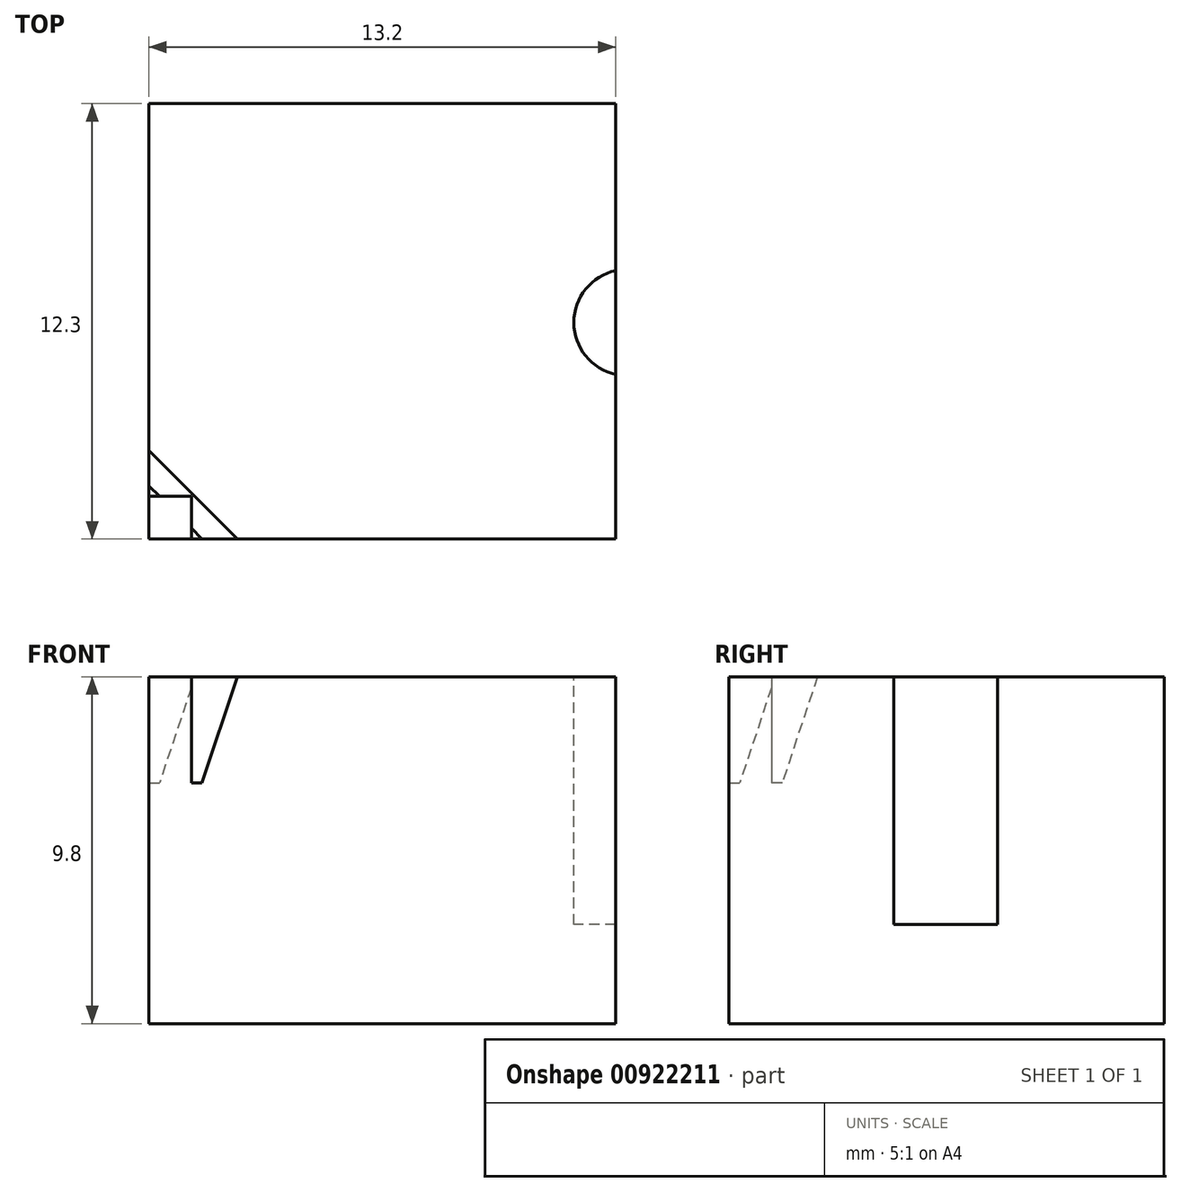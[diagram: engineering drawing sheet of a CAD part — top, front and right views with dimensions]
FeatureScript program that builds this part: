
annotation { "Feature Type Name" : "Feature", "Feature Type Description" : "" }
export const myFeature = defineFeature(function(context is Context, id is Id, definition is map)
    precondition{}
    {
        {
            var Q0;
            Q0=qCreatedBy(makeId("Top.planeOp"),FACE);
            var sketch = newSketch(context, id + "F0", { "sketchPlane" : qUnion([Q0])});
            skLineSegment(sketch, "E0.bottom", {"start": v(-6.6, 6.15) * mm, "end": v(6.6, 6.15) * mm});
            skLineSegment(sketch, "E0.top", {"start": v(-6.6, -6.15) * mm, "end": v(6.6, -6.15) * mm});
            skLineSegment(sketch, "E0.left", {"start": v(-6.6, 6.15) * mm, "end": v(-6.6, -6.15) * mm});
            skLineSegment(sketch, "E0.right", {"start": v(6.6, 6.15) * mm, "end": v(6.6, -6.15) * mm});
            skPoint(sketch, "E0.middle", {"position": v(0, 0) * mm});
            skSolve(sketch);
        }
        {
            var Q0;
            Q0 = qSketchRegion(id + "F0", true);
            extrude(context, id + "F1", {"entities" : qUnion([Q0]), "depth" : 9.8 * mm, "offsetDistance" : 25 * mm});
        }
        {
            var Q0;
            Q0=qCreatedBy(makeId("Top.planeOp"),FACE);
            cPlane(context, id + "F2", {"entities" : qUnion([Q0]), "cplaneType" : CPlaneType.OFFSET, "offset" : 6.8 * mm, "width" : 150 * mm, "height" : 150 * mm});
        }
        {
            var Q0;
            Q0=makeQuery(id+"F1.opExtrude","CAP_FACE",FACE,{"disambiguationData":[OSD([sQuery(id+"F0.wireOp",EDGE,"E0.bottom"),sQuery(id+"F0.wireOp",EDGE,"E0.top"),sQuery(id+"F0.wireOp",EDGE,"E0.left"),sQuery(id+"F0.wireOp",EDGE,"E0.right")])],"isStart":false});
            var sketch = newSketch(context, id + "F3", { "sketchPlane" : qUnion([Q0])});
            skLineSegment(sketch, "E1", {"start": v(-6.6, -6.15) * mm, "end": v(-4.1, -6.15) * mm});
            skLineSegment(sketch, "E2", {"start": v(-4.1, -6.15) * mm, "end": v(-6.6, -3.65) * mm});
            skLineSegment(sketch, "E3", {"start": v(-6.6, -3.65) * mm, "end": v(-6.6, -6.15) * mm});
            skSolve(sketch);
        }
        {
            var Q0;
            Q0=qCreatedBy(id+"F2.planeOp",FACE);
            var sketch = newSketch(context, id + "F4", { "sketchPlane" : qUnion([Q0])});
            skLineSegment(sketch, "E4", {"start": v(-5.1, -6.15) * mm, "end": v(-6.6, -4.65) * mm});
            skLineSegment(sketch, "E5", {"start": v(-6.6, -4.65) * mm, "end": v(-6.6, -6.15) * mm});
            skLineSegment(sketch, "E6", {"start": v(-6.6, -6.15) * mm, "end": v(-5.1, -6.15) * mm});
            skSolve(sketch);
        }
        {
            var Q1;
            Q1 = qSketchRegion(id + "F3", true);
            var Q2;
            Q2 = qSketchRegion(id + "F4", true);
            loft(context, id + "F5", {"operationType" : NewBodyOperationType.REMOVE, "sheetProfilesArray" : [{ "sheetProfileEntities" : qUnion([Q1]) }, { "sheetProfileEntities" : qUnion([Q2]) }]});
        }
        {
            var Q0;
            Q0=makeQuery(id+"F5.boolean.opBoolean","COPY",FACE,{"derivedFrom":makeQuery(id+"F5.opLoft","CAP_FACE",FACE,{"disambiguationData":[OSD([makeQuery(id+"F4.imprint","IMPRINT",FACE,{"disambiguationData":[TD([[makeQuery(id+"F4.imprint","IMPRINT",EDGE,{"derivedFrom":sQuery(id+"F4.wireOp",EDGE,"E4")}),1.0]])]})])],"isStart":true})});
            var sketch = newSketch(context, id + "F6", { "sketchPlane" : qUnion([Q0])});
            skLineSegment(sketch, "E7.bottom", {"start": v(-6.6, -6.15) * mm, "end": v(-5.4, -6.15) * mm});
            skLineSegment(sketch, "E7.top", {"start": v(-6.6, -4.95) * mm, "end": v(-5.4, -4.95) * mm});
            skLineSegment(sketch, "E7.left", {"start": v(-6.6, -6.15) * mm, "end": v(-6.6, -4.95) * mm});
            skLineSegment(sketch, "E7.right", {"start": v(-5.4, -6.15) * mm, "end": v(-5.4, -4.95) * mm});
            skSolve(sketch);
        }
        {
            var Q0;
            Q0 = qSketchRegion(id + "F6", true);
            extrude(context, id + "F7", {"entities" : qUnion([Q0]), "operationType" : NewBodyOperationType.ADD, "depth" : 3 * mm, "offsetDistance" : 25 * mm});
        }
        {
            var Q0;
            Q0=makeQuery(id+"F1.opExtrude","CAP_FACE",FACE,{"disambiguationData":[OSD([sQuery(id+"F0.wireOp",EDGE,"E0.bottom"),sQuery(id+"F0.wireOp",EDGE,"E0.top"),sQuery(id+"F0.wireOp",EDGE,"E0.left"),sQuery(id+"F0.wireOp",EDGE,"E0.right")])],"isStart":false});
            var sketch = newSketch(context, id + "F8", { "sketchPlane" : qUnion([Q0])});
            skArc(sketch, "E8", {"start": v(6.6, 1.43) * mm, "mid": v(5.41, -0.03) * mm, "end": v(6.6, -1.5) * mm});
            skLineSegment(sketch, "E9", {"start": v(6.6, -1.5) * mm, "end": v(6.6, 1.43) * mm});
            skSolve(sketch);
        }
        {
            var Q0;
            Q0 = qSketchRegion(id + "F8", true);
            extrude(context, id + "F9", {"entities" : qUnion([Q0]), "operationType" : NewBodyOperationType.REMOVE, "oppositeDirection" : true, "depth" : 7 * mm, "offsetDistance" : 25 * mm});
        }
    });
